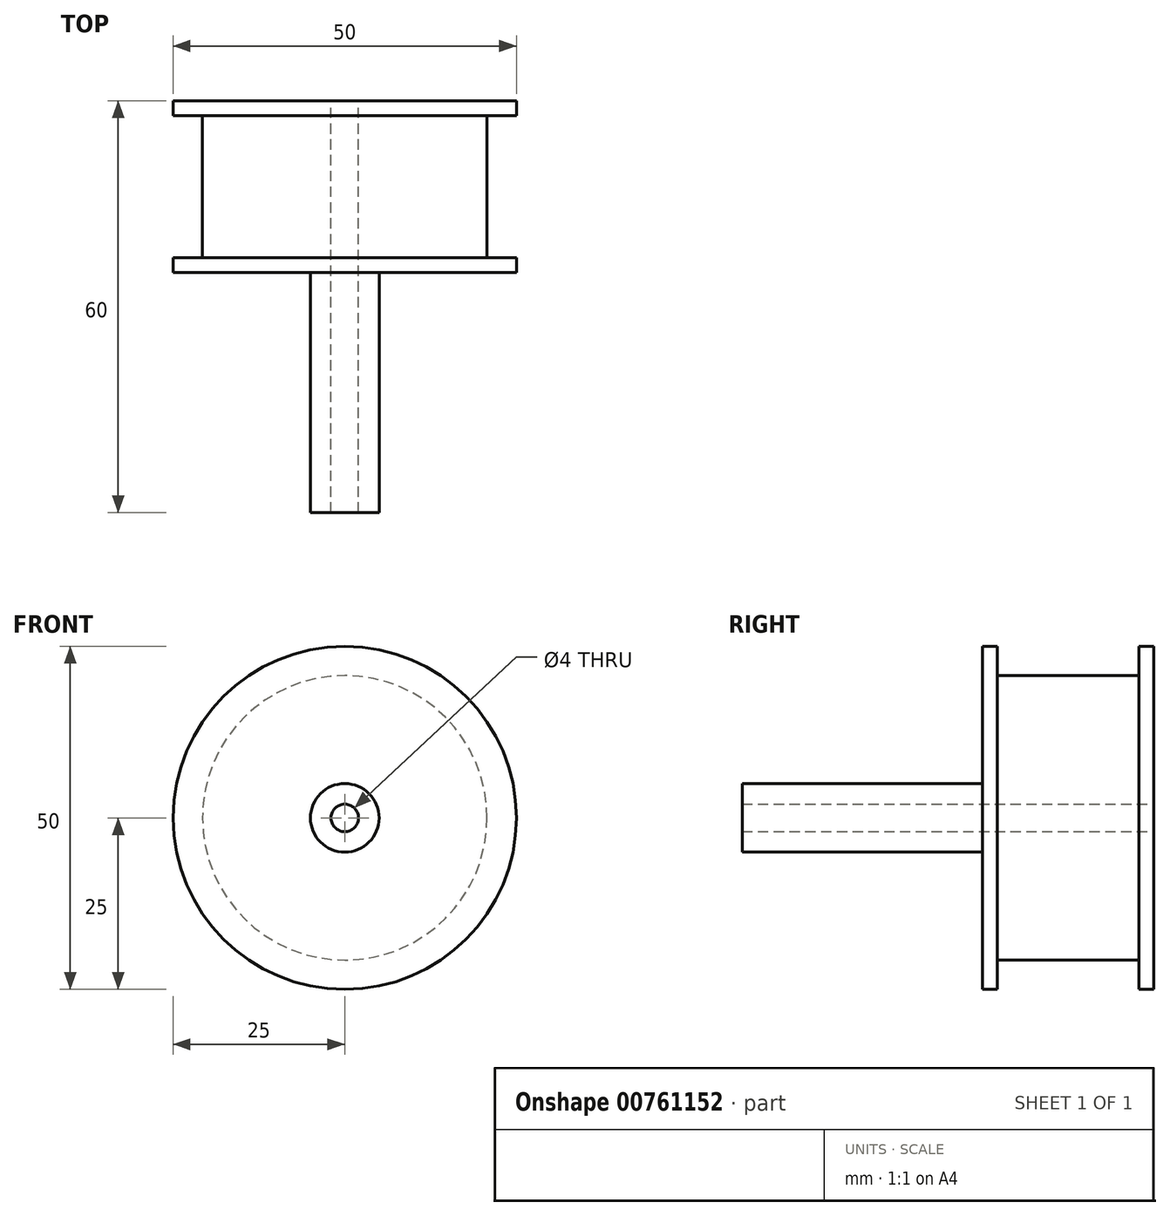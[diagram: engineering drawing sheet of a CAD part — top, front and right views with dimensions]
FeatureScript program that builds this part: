
annotation { "Feature Type Name" : "Feature", "Feature Type Description" : "" }
export const myFeature = defineFeature(function(context is Context, id is Id, definition is map)
    precondition{}
    {
        {
            var Q0;
            Q0=qCreatedBy(makeId("Front.planeOp"),FACE);
            var sketch = newSketch(context, id + "F0", { "sketchPlane" : qUnion([Q0])});
            skCircle(sketch, "E0", {"center": v(0, 0) * mm, "radius": 25 * mm});
            skCircle(sketch, "E1", {"center": v(0, 0) * mm, "radius": 2 * mm});
            skCircle(sketch, "E2", {"center": v(0, 0) * mm, "radius": 5 * mm});
            skSolve(sketch);
        }
        {
            var Q0;
            Q0=makeQuery(id+"F0.imprint","IMPRINT",FACE,{"disambiguationData":[TD([[makeQuery(id+"F0.imprint","IMPRINT",EDGE,{"derivedFrom":sQuery(id+"F0.wireOp",EDGE,"E0")}),1.0]])]});
            extrude(context, id + "F1", {"entities" : qUnion([Q0]), "depth" : 25 * mm, "offsetDistance" : 25 * mm});
        }
        {
            var Q0;
            Q0=makeQuery(id+"F0.imprint","IMPRINT",FACE,{"disambiguationData":[TD([[makeQuery(id+"F0.imprint","IMPRINT",EDGE,{"derivedFrom":sQuery(id+"F0.wireOp",EDGE,"E1")}),-1.0]])]});
            extrude(context, id + "F2", {"entities" : qUnion([Q0]), "operationType" : NewBodyOperationType.ADD, "depth" : 60 * mm, "offsetDistance" : 25 * mm});
        }
        {
            var Q0;
            Q0=qCreatedBy(makeId("Right.planeOp"),FACE);
            var sketch = newSketch(context, id + "F3", { "sketchPlane" : qUnion([Q0])});
            skLineSegment(sketch, "E3", {"start": v(-2.17, 26.64) * mm, "end": v(-2.17, 20.73) * mm});
            skLineSegment(sketch, "E4", {"start": v(-2.17, 20.73) * mm, "end": v(-22.84, 20.73) * mm});
            skLineSegment(sketch, "E5", {"start": v(-22.84, 20.73) * mm, "end": v(-22.84, 26.71) * mm});
            skLineSegment(sketch, "E6", {"start": v(-2.17, 26.64) * mm, "end": v(-22.84, 26.71) * mm});
            skLineSegment(sketch, "E7", {"start": v(0, 0) * mm, "end": v(-68.68, 0) * mm});
            skSolve(sketch);
        }
        {
            var Q0;
            Q0=makeQuery(id+"F3.imprint","IMPRINT",FACE,{"disambiguationData":[TD([[makeQuery(id+"F3.imprint","IMPRINT",EDGE,{"derivedFrom":sQuery(id+"F3.wireOp",EDGE,"E3")}),-1.0]])]});
            var Q1;
            Q1=sQuery(id+"F3.wireOp",EDGE,"E7");
            revolve(context, id + "F4", {"operationType" : NewBodyOperationType.REMOVE, "surfaceOperationType" : NewSurfaceOperationType.NEW, "entities" : qUnion([Q0]), "axis" : qUnion([Q1]), "revolveType" : RevolveType.FULL});
        }
    });
